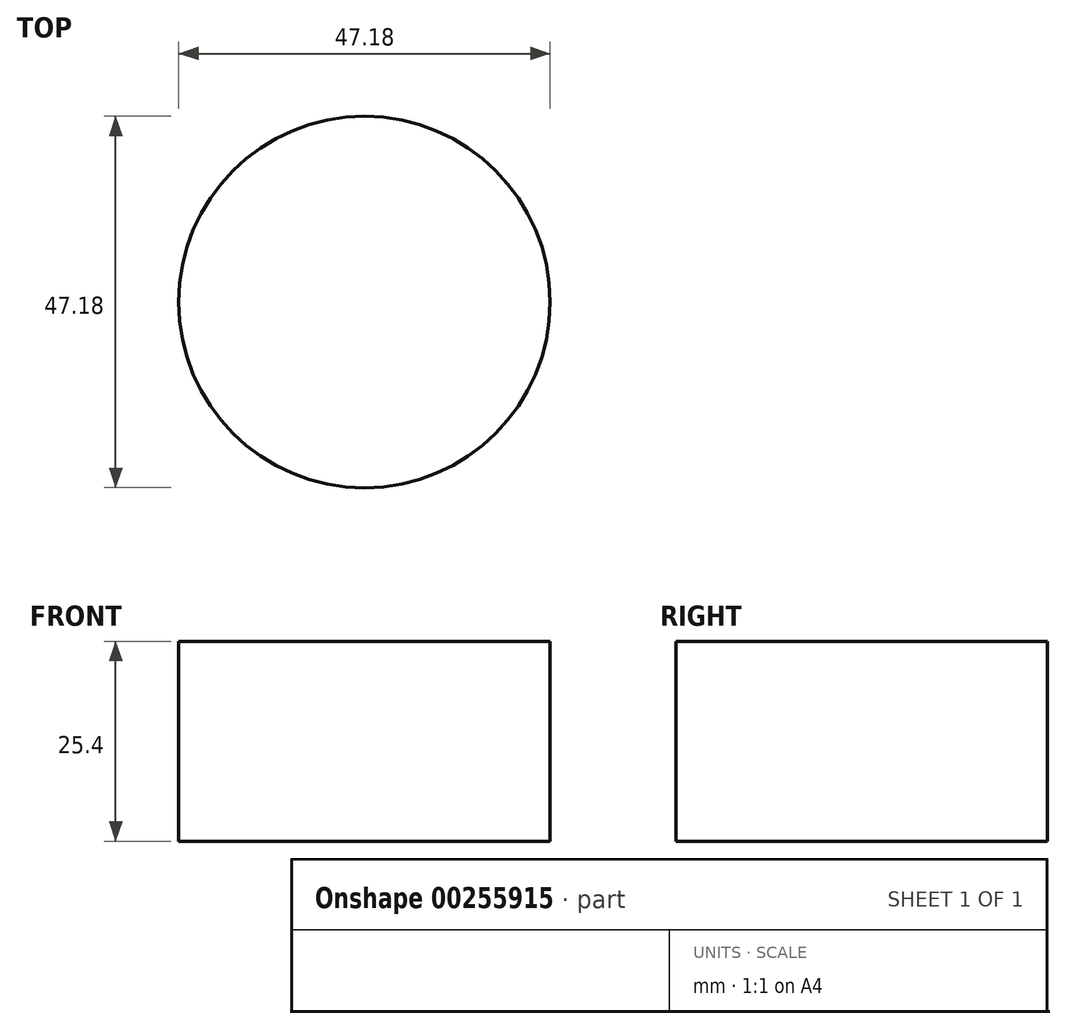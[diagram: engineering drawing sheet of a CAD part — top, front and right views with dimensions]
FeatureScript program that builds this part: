
annotation { "Feature Type Name" : "Feature", "Feature Type Description" : "" }
export const myFeature = defineFeature(function(context is Context, id is Id, definition is map)
    precondition{}
    {
        {
            var Q0;
            Q0=qCreatedBy(makeId("Top.planeOp"),FACE);
            var sketch = newSketch(context, id + "F0", { "sketchPlane" : qUnion([Q0])});
            skCircle(sketch, "E0", {"center": v(0, 0) * mm, "radius": 23.6 * mm});
            skSolve(sketch);
        }
        {
            var Q0;
            Q0=sQuery(id+"F0.wireOp",EDGE,"E0");
            extrude(context, id + "F1", {"bodyType" : ToolBodyType.SURFACE, "surfaceEntities" : qUnion([Q0]), "depth" : 25.4 * mm});
        }
    });
